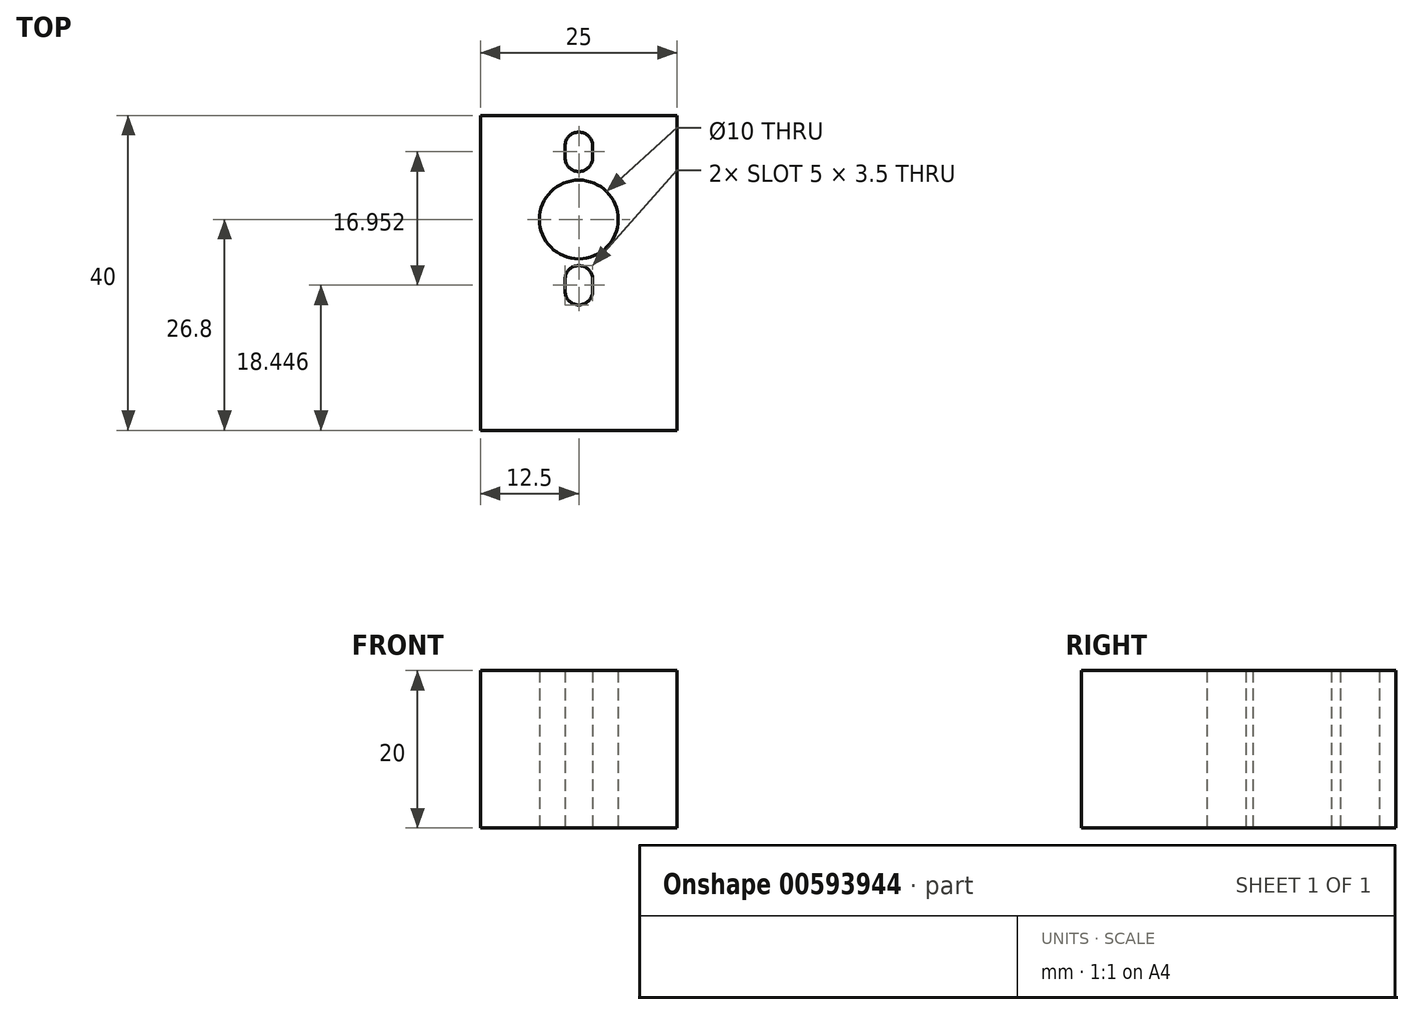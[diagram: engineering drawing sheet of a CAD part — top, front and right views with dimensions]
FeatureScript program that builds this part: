
annotation { "Feature Type Name" : "Feature", "Feature Type Description" : "" }
export const myFeature = defineFeature(function(context is Context, id is Id, definition is map)
    precondition{}
    {
        {
            var Q0;
            Q0=qCreatedBy(makeId("Top.planeOp"),FACE);
            var sketch = newSketch(context, id + "F0", { "sketchPlane" : qUnion([Q0])});
            skPoint(sketch, "E0.middle", {"position": v(0, 1) * mm});
            skCircle(sketch, "E1", {"center": v(0, 8.04) * mm, "radius": 5 * mm});
            skPoint(sketch, "E1.centerSnap0", {"position": v(0, 21.5) * mm});
            skLineSegment(sketch, "E2.bottom", {"start": v(0, 14.14) * mm, "end": v(0, 14.14) * mm});
            skLineSegment(sketch, "E2.top", {"start": v(0, 19.14) * mm, "end": v(0, 19.14) * mm});
            skLineSegment(sketch, "E2.left", {"start": v(1.75, 15.89) * mm, "end": v(1.75, 17.39) * mm});
            skLineSegment(sketch, "E2.right", {"start": v(-1.75, 15.89) * mm, "end": v(-1.75, 17.39) * mm});
            skPoint(sketch, "E2.middle", {"position": v(0, 16.64) * mm});
            skLineSegment(sketch, "E3.bottom", {"start": v(0, -3.81) * mm, "end": v(0, -3.81) * mm});
            skLineSegment(sketch, "E3.top", {"start": v(0, 1.19) * mm, "end": v(0, 1.19) * mm});
            skLineSegment(sketch, "E3.left", {"start": v(1.75, -1.06) * mm, "end": v(1.75, 0.44) * mm});
            skLineSegment(sketch, "E3.right", {"start": v(-1.75, -1.06) * mm, "end": v(-1.75, 0.44) * mm});
            skPoint(sketch, "E3.middle", {"position": v(0, -0.31) * mm});
            skPoint(sketch, "E4.visualSharp", {"position": v(-1.75, 19.14) * mm});
            skArc(sketch, "E4.filletArc", {"start": v(0, 19.14) * mm, "mid": v(-1.24, 18.63) * mm, "end": v(-1.75, 17.39) * mm});
            skPoint(sketch, "E5.visualSharp", {"position": v(1.75, 19.14) * mm});
            skArc(sketch, "E5.filletArc", {"start": v(1.75, 17.39) * mm, "mid": v(1.24, 18.63) * mm, "end": v(0, 19.14) * mm});
            skPoint(sketch, "E6.visualSharp", {"position": v(1.75, 14.14) * mm});
            skArc(sketch, "E6.filletArc", {"start": v(0, 14.14) * mm, "mid": v(1.24, 14.65) * mm, "end": v(1.75, 15.89) * mm});
            skPoint(sketch, "E7.visualSharp", {"position": v(-1.75, 14.14) * mm});
            skArc(sketch, "E7.filletArc", {"start": v(-1.75, 15.89) * mm, "mid": v(-1.24, 14.65) * mm, "end": v(0, 14.14) * mm});
            skPoint(sketch, "E8.visualSharp", {"position": v(-1.75, 2.19) * mm});
            skArc(sketch, "E8.filletArc", {"start": v(0, 2.19) * mm, "mid": v(-1.24, 1.67) * mm, "end": v(-1.75, 0.44) * mm});
            skPoint(sketch, "E9.visualSharp", {"position": v(1.75, 2.19) * mm});
            skArc(sketch, "E9.filletArc", {"start": v(1.75, 0.44) * mm, "mid": v(1.24, 1.67) * mm, "end": v(0, 2.19) * mm});
            skPoint(sketch, "E10.visualSharp", {"position": v(-1.75, -2.81) * mm});
            skArc(sketch, "E10.filletArc", {"start": v(-1.75, -1.06) * mm, "mid": v(-1.24, -2.3) * mm, "end": v(0, -2.81) * mm});
            skPoint(sketch, "E11.visualSharp", {"position": v(1.75, -2.81) * mm});
            skArc(sketch, "E11.filletArc", {"start": v(0, -2.81) * mm, "mid": v(1.24, -2.3) * mm, "end": v(1.75, -1.06) * mm});
            skLineSegment(sketch, "E12.bottom", {"start": v(12.5, -18.76) * mm, "end": v(-12.5, -18.76) * mm});
            skLineSegment(sketch, "E12.top", {"start": v(12.5, 21.24) * mm, "end": v(-12.5, 21.24) * mm});
            skLineSegment(sketch, "E12.left", {"start": v(12.5, -18.76) * mm, "end": v(12.5, 21.24) * mm});
            skLineSegment(sketch, "E12.right", {"start": v(-12.5, -18.76) * mm, "end": v(-12.5, 21.24) * mm});
            skSolve(sketch);
        }
        {
            var Q0;
            Q0=makeQuery(id+"F0.imprint","IMPRINT",FACE,{"disambiguationData":[TD([[makeQuery(id+"F0.imprint","IMPRINT",EDGE,{"derivedFrom":sQuery(id+"F0.wireOp",EDGE,"E1")}),-1.0]])]});
            extrude(context, id + "F1", {"entities" : qUnion([Q0]), "depth" : 20 * mm, "offsetDistance" : 25 * mm});
        }
    });
